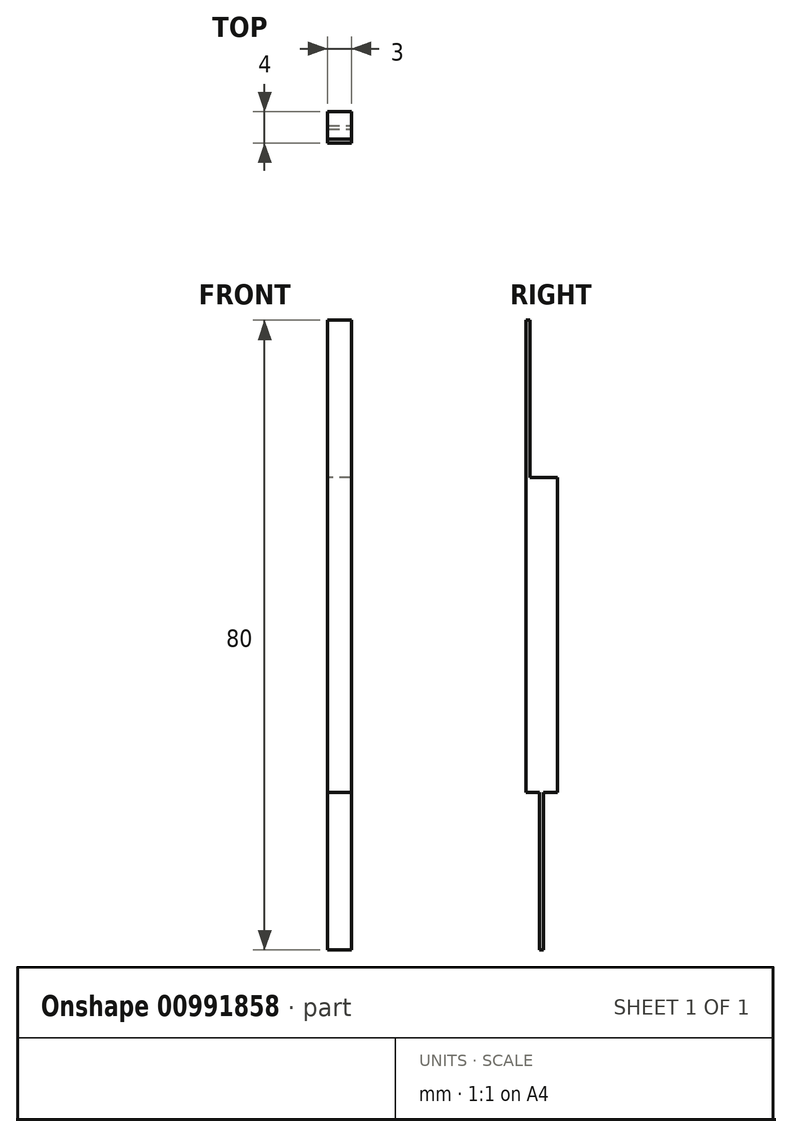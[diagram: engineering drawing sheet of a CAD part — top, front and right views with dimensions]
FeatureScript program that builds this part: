
annotation { "Feature Type Name" : "Feature", "Feature Type Description" : "" }
export const myFeature = defineFeature(function(context is Context, id is Id, definition is map)
    precondition{}
    {
        {
            var Q0;
            Q0=qCreatedBy(makeId("Front.planeOp"),FACE);
            var sketch = newSketch(context, id + "F0", { "sketchPlane" : qUnion([Q0])});
            skLineSegment(sketch, "E0.bottom", {"start": v(-1.5, -40) * mm, "end": v(1.5, -40) * mm});
            skLineSegment(sketch, "E0.top", {"start": v(-1.5, -20) * mm, "end": v(1.5, -20) * mm});
            skLineSegment(sketch, "E0.left", {"start": v(-1.5, -40) * mm, "end": v(-1.5, -20) * mm});
            skLineSegment(sketch, "E0.right", {"start": v(1.5, -40) * mm, "end": v(1.5, -20) * mm});
            skPoint(sketch, "E0.middle", {"position": v(0, -30) * mm});
            skSolve(sketch);
        }
        {
            var Q0;
            Q0=makeQuery(id+"F0.imprint","IMPRINT",FACE,{"disambiguationData":[TD([[makeQuery(id+"F0.imprint","IMPRINT",EDGE,{"derivedFrom":sQuery(id+"F0.wireOp",EDGE,"E0.bottom")}),1.0]])]});
            extrude(context, id + "F1", {"entities" : qUnion([Q0]), "oppositeDirection" : true, "depth" : 0.5 * mm, "offsetDistance" : 25 * mm, "symmetric" : true});
        }
        {
            var Q0;
            Q0=qCreatedBy(makeId("Front.planeOp"),FACE);
            var sketch = newSketch(context, id + "F2", { "sketchPlane" : qUnion([Q0])});
            skLineSegment(sketch, "E1.bottom", {"start": v(-1.5, -20) * mm, "end": v(1.5, -20) * mm});
            skLineSegment(sketch, "E1.top", {"start": v(-1.5, 20) * mm, "end": v(1.5, 20) * mm});
            skLineSegment(sketch, "E1.left", {"start": v(-1.5, -20) * mm, "end": v(-1.5, 20) * mm});
            skLineSegment(sketch, "E1.right", {"start": v(1.5, -20) * mm, "end": v(1.5, 20) * mm});
            skPoint(sketch, "E1.middle", {"position": v(0, 0) * mm});
            skSolve(sketch);
        }
        {
            var Q0;
            Q0 = qSketchRegion(id + "F2", true);
            extrude(context, id + "F3", {"entities" : qUnion([Q0]), "operationType" : NewBodyOperationType.ADD, "depth" : 4 * mm, "offsetDistance" : 25 * mm, "symmetric" : true});
        }
        {
            var Q0;
            Q0=qCreatedBy(makeId("Front.planeOp"),FACE);
            var sketch = newSketch(context, id + "F4", { "sketchPlane" : qUnion([Q0])});
            skLineSegment(sketch, "E2.bottom", {"start": v(1.5, 40) * mm, "end": v(-1.5, 40) * mm});
            skLineSegment(sketch, "E2.top", {"start": v(1.5, 20) * mm, "end": v(-1.5, 20) * mm});
            skLineSegment(sketch, "E2.left", {"start": v(1.5, 40) * mm, "end": v(1.5, 20) * mm});
            skLineSegment(sketch, "E2.right", {"start": v(-1.5, 40) * mm, "end": v(-1.5, 20) * mm});
            skPoint(sketch, "E2.middle", {"position": v(0, 30) * mm});
            skSolve(sketch);
        }
        {
            var Q0;
            Q0 = qSketchRegion(id + "F4", true);
            extrude(context, id + "F5", {"entities" : qUnion([Q0]), "operationType" : NewBodyOperationType.ADD, "depth" : 2 * mm, "offsetDistance" : 25 * mm});
        }
        {
            var Q0;
            Q0 = qSketchRegion(id + "F4", true);
            extrude(context, id + "F6", {"entities" : qUnion([Q0]), "operationType" : NewBodyOperationType.REMOVE, "depth" : 1.5 * mm, "offsetDistance" : 25 * mm});
        }
    });
